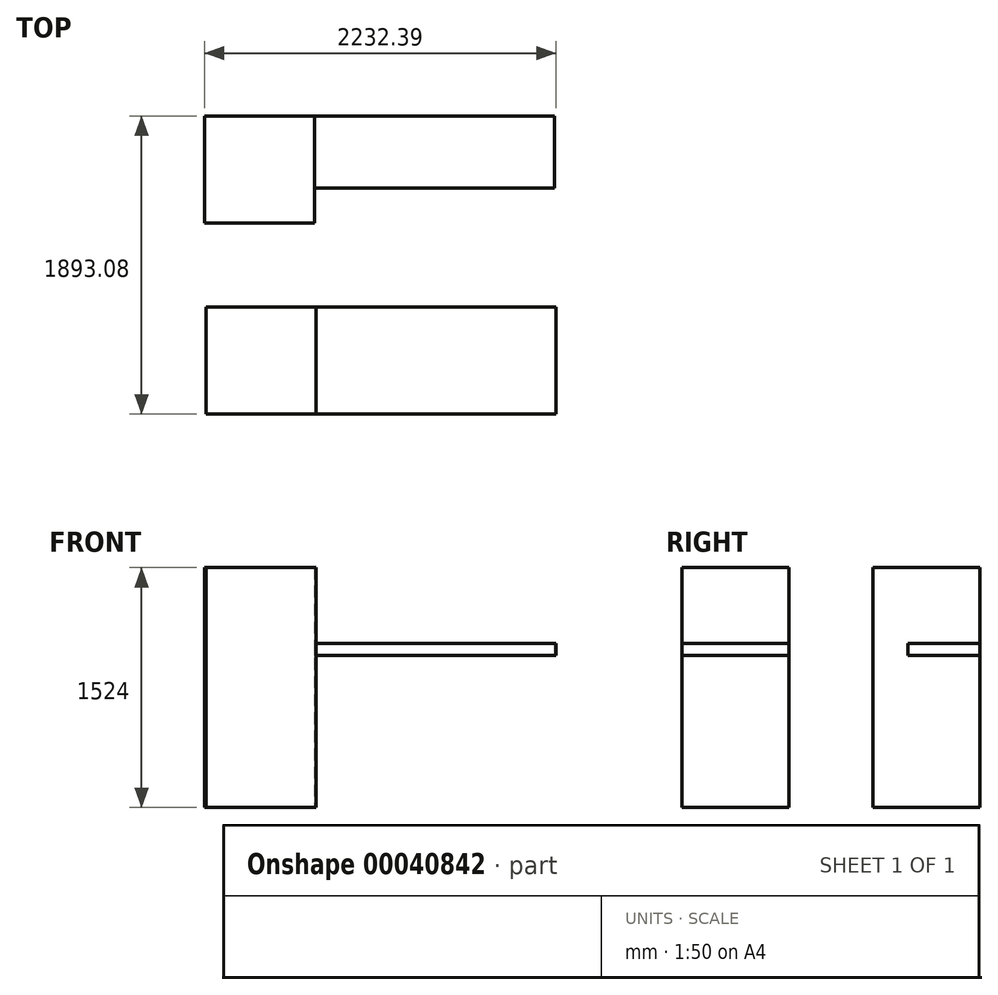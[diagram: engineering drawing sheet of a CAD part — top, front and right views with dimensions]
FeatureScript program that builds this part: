
annotation { "Feature Type Name" : "Feature", "Feature Type Description" : "" }
export const myFeature = defineFeature(function(context is Context, id is Id, definition is map)
    precondition{}
    {
        {
            var Q0;
            Q0=qCreatedBy(makeId("Top.planeOp"),FACE);
            var sketch = newSketch(context, id + "F0", { "sketchPlane" : qUnion([Q0])});
            skLineSegment(sketch, "E0.bottom", {"start": v(-1043.72, 581.5) * mm, "end": v(-345.22, 581.5) * mm});
            skLineSegment(sketch, "E0.top", {"start": v(-1043.72, -97.95) * mm, "end": v(-345.22, -97.95) * mm});
            skLineSegment(sketch, "E0.left", {"start": v(-1043.72, 581.5) * mm, "end": v(-1043.72, -97.95) * mm});
            skLineSegment(sketch, "E0.right", {"start": v(-345.22, 581.5) * mm, "end": v(-345.22, -97.95) * mm});
            skLineSegment(sketch, "E1.bottom", {"start": v(-345.22, 581.5) * mm, "end": v(1178.78, 581.5) * mm});
            skLineSegment(sketch, "E1.top", {"start": v(-345.22, 124.3) * mm, "end": v(1178.78, 124.3) * mm});
            skLineSegment(sketch, "E1.left", {"start": v(-345.22, 581.5) * mm, "end": v(-345.22, 124.3) * mm});
            skLineSegment(sketch, "E1.right", {"start": v(1178.78, 581.5) * mm, "end": v(1178.78, 124.3) * mm});
            skLineSegment(sketch, "E2.top", {"start": v(-335.33, -1311.58) * mm, "end": v(1188.67, -1311.58) * mm});
            skLineSegment(sketch, "E2.bottom", {"start": v(-335.33, -632.13) * mm, "end": v(1188.67, -632.13) * mm});
            skLineSegment(sketch, "E3.left", {"start": v(-1033.83, -632.13) * mm, "end": v(-1033.83, -1311.58) * mm});
            skLineSegment(sketch, "E3.top", {"start": v(-1033.83, -1311.58) * mm, "end": v(-335.33, -1311.58) * mm});
            skLineSegment(sketch, "E3.bottom", {"start": v(-1033.83, -632.13) * mm, "end": v(-335.33, -632.13) * mm});
            skLineSegment(sketch, "E2.right", {"start": v(1188.67, -632.13) * mm, "end": v(1188.67, -1311.58) * mm});
            skLineSegment(sketch, "E4.bottom", {"start": v(-304.39, 1625.56) * mm, "end": v(1219.61, 1625.56) * mm});
            skLineSegment(sketch, "E4.top", {"start": v(-304.39, 914.36) * mm, "end": v(1219.61, 914.36) * mm});
            skLineSegment(sketch, "E4.left", {"start": v(-304.39, 1625.56) * mm, "end": v(-304.39, 914.36) * mm});
            skLineSegment(sketch, "E4.right", {"start": v(1219.61, 1625.56) * mm, "end": v(1219.61, 914.36) * mm});
            skText(sketch, "E5", { "text": "desk", "fontName": "OpenSans-Regular.ttf"});
            skText(sketch, "E6", { "text": "current", "fontName": "OpenSans-Regular.ttf"});
            skText(sketch, "E7", { "text": "new", "fontName": "OpenSans-Regular.ttf"});
            const initialGuessF0  = {"E5": [-1.13457, 1.35021, 1, 0, 0.1816], "E6": [-2.494, 0.27097, 1, 0, 0.26981], "E7": [-2.05297, -0.82384, 1, 0, 0.25943]};
            skSetInitialGuess(sketch, initialGuessF0);
            skSolve(sketch);
        }
        {
            var Q0;
            Q0=makeQuery(id+"F0.imprint","IMPRINT",FACE,{"disambiguationData":[TD([[makeQuery(id+"F0.imprint","IMPRINT",EDGE,{"derivedFrom":sQuery(id+"F0.wireOp",EDGE,"E2.top")}),1.0]])]});
            var Q1;
            Q1=makeQuery(id+"F0.imprint","IMPRINT",FACE,{"disambiguationData":[TD([[makeQuery(id+"F0.imprint","IMPRINT",EDGE,{"derivedFrom":sQuery(id+"F0.wireOp",EDGE,"E1.bottom")}),-1.0]])]});
            extrude(context, id + "F1", {"entities" : qUnion([Q0, Q1]), "depth" : 1041.4 * mm, "hasSecondDirection" : true, "secondDirectionOppositeDirection" : false, "secondDirectionDepth" : 965.2 * mm});
        }
        {
            var Q0;
            Q0=makeQuery(id+"F0.imprint","IMPRINT",FACE,{"disambiguationData":[TD([[makeQuery(id+"F0.imprint","IMPRINT",EDGE,{"derivedFrom":sQuery(id+"F0.wireOp",EDGE,"E3.left")}),1.0]])]});
            var Q1;
            Q1=makeQuery(id+"F0.imprint","IMPRINT",FACE,{"disambiguationData":[TD([[makeQuery(id+"F0.imprint","IMPRINT",EDGE,{"derivedFrom":sQuery(id+"F0.wireOp",EDGE,"E0.bottom")}),-1.0]])]});
            extrude(context, id + "F2", {"entities" : qUnion([Q0, Q1]), "depth" : 1524 * mm});
        }
    });
